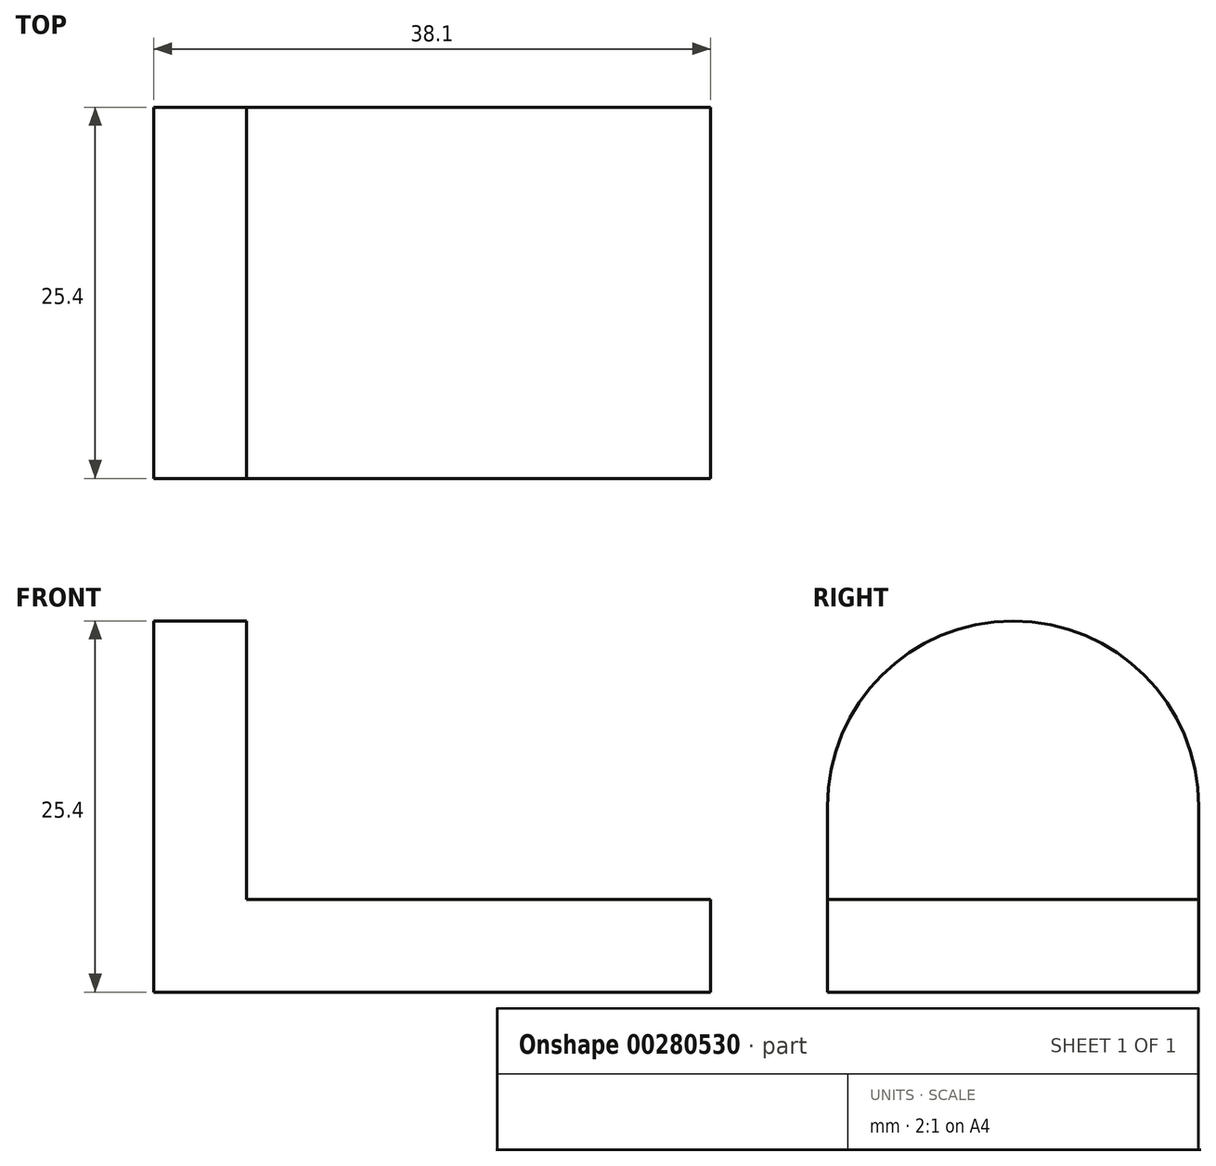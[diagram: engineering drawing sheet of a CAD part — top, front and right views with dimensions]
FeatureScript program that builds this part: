
annotation { "Feature Type Name" : "Feature", "Feature Type Description" : "" }
export const myFeature = defineFeature(function(context is Context, id is Id, definition is map)
    precondition{}
    {
        {
            var Q0;
            Q0=qCreatedBy(makeId("Right.planeOp"),FACE);
            var sketch = newSketch(context, id + "F0", { "sketchPlane" : qUnion([Q0])});
            skLineSegment(sketch, "E0.bottom", {"start": v(0, 0) * mm, "end": v(-25.4, 0) * mm});
            skLineSegment(sketch, "E0.top", {"start": v(0, 6.35) * mm, "end": v(-25.4, 6.35) * mm});
            skLineSegment(sketch, "E0.left", {"start": v(0, 0) * mm, "end": v(0, 6.35) * mm});
            skLineSegment(sketch, "E0.right", {"start": v(-25.4, 0) * mm, "end": v(-25.4, 6.35) * mm});
            skSolve(sketch);
        }
        {
            var Q0;
            Q0 = qSketchRegion(id + "F0", true);
            extrude(context, id + "F1", {"entities" : qUnion([Q0]), "depth" : 38.1 * mm});
        }
        {
            var Q0;
            Q0=qCreatedBy(makeId("Right.planeOp"),FACE);
            var sketch = newSketch(context, id + "F2", { "sketchPlane" : qUnion([Q0])});
            skLineSegment(sketch, "E1.bottom", {"start": v(0, 6.35) * mm, "end": v(-25.4, 6.35) * mm});
            skLineSegment(sketch, "E1.top", {"start": v(0, 12.7) * mm, "end": v(-25.4, 12.7) * mm});
            skLineSegment(sketch, "E1.left", {"start": v(0, 6.35) * mm, "end": v(0, 12.7) * mm});
            skLineSegment(sketch, "E1.right", {"start": v(-25.4, 6.35) * mm, "end": v(-25.4, 12.7) * mm});
            skSolve(sketch);
        }
        {
            var Q0;
            Q0 = qSketchRegion(id + "F2", true);
            extrude(context, id + "F3", {"entities" : qUnion([Q0]), "operationType" : NewBodyOperationType.ADD, "depth" : 6.35 * mm});
        }
        {
            var Q0;
            Q0=qCreatedBy(makeId("Right.planeOp"),FACE);
            var sketch = newSketch(context, id + "F4", { "sketchPlane" : qUnion([Q0])});
            skArc(sketch, "E2", {"start": v(0, 12.7) * mm, "mid": v(-12.7, 25.4) * mm, "end": v(-25.4, 12.7) * mm});
            skLineSegment(sketch, "E3", {"start": v(-25.4, 12.7) * mm, "end": v(0, 12.7) * mm});
            skSolve(sketch);
        }
        {
            var Q0;
            Q0=makeQuery(id+"F4.imprint","IMPRINT",FACE,{"disambiguationData":[TD([[makeQuery(id+"F4.imprint","IMPRINT",EDGE,{"derivedFrom":sQuery(id+"F4.wireOp",EDGE,"E2")}),1.0]])]});
            extrude(context, id + "F5", {"entities" : qUnion([Q0]), "operationType" : NewBodyOperationType.ADD, "depth" : 6.35 * mm});
        }
    });
